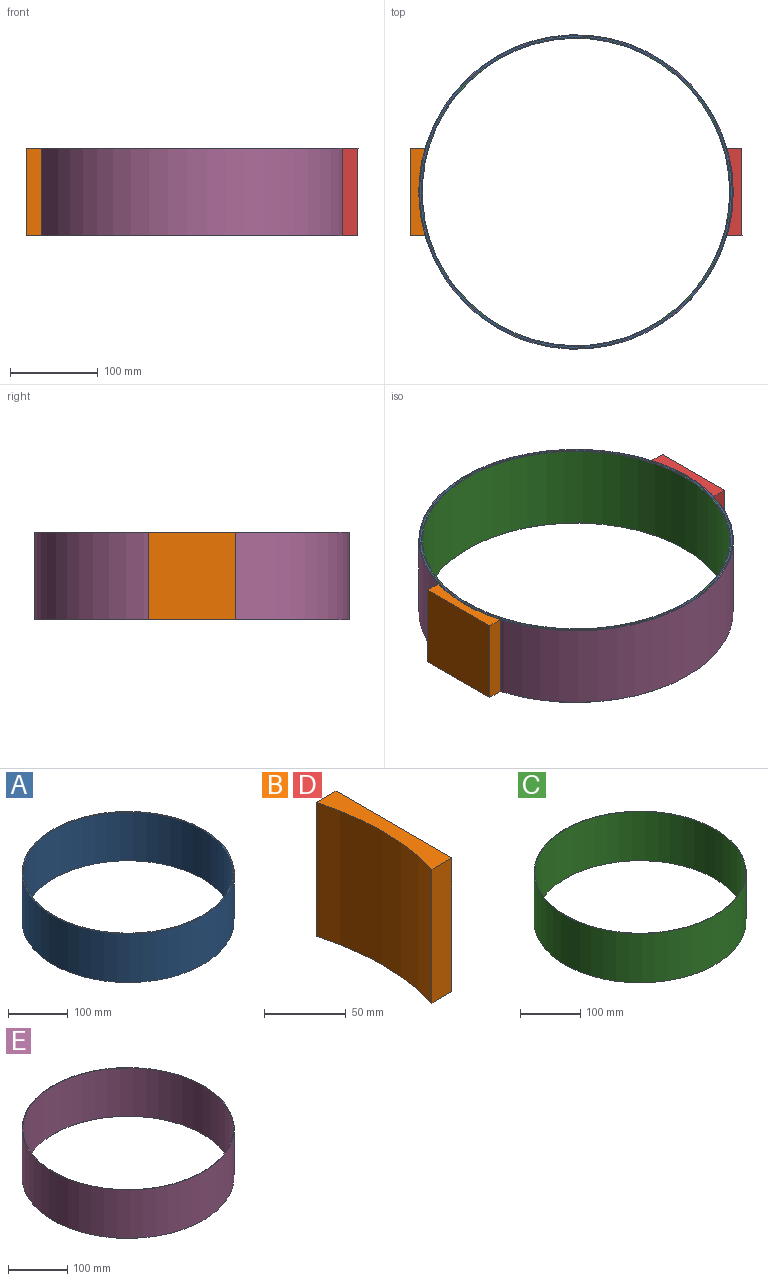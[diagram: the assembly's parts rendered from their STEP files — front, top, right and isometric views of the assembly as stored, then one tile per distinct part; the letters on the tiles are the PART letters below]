
ASSEMBLY  parts=5 mates=7
PART A: 4 faces, bbox 356x356x100 mm
  f0: cylinder r=176mm len=352mm, axis (0,0,-1), area 110584.1mm2, adj f2,f3
  f1: cylinder r=178mm len=356mm, axis (0,0,-1), area 111840.7mm2, adj f2,f3
  f2: plane 356x356mm, normal (0,0,1), area 2224.2mm2, adj f0,f1
  f3: plane 356x356mm, normal (0,0,-1), area 2224.2mm2, adj f0,f1
PART B: 6 faces, bbox 17.1x100x100 mm
  f0: plane 100x100mm, normal (1,0,0), area 10000mm2, adj f1,f3,f4,f5
  f1: plane 100x17.13mm, normal (0,1,0), area 1712.5mm2, adj f0,f2,f4,f5
  f2: cylinder r=179mm len=100mm, axis (0,0,-1), area 10134.8mm2, adj f1,f3,f4,f5
  f3: plane 100x17.13mm, normal (0,-1,0), area 1712.5mm2, adj f0,f2,f4,f5
  f4: plane 100x17.13mm, normal (0,0,1), area 1235.6mm2, adj f0,f1,f2,f3
  f5: plane 100x17.13mm, normal (0,0,-1), area 1235.6mm2, adj f0,f1,f2,f3
PART C: 4 faces, bbox 352x352x100 mm
  f0: cylinder r=175mm len=350mm, axis (0,0,-1), area 109955.7mm2, adj f2,f3
  f1: cylinder r=176mm len=352mm, axis (0,0,-1), area 110584.1mm2, adj f2,f3
  f2: plane 352x352mm, normal (0,0,1), area 1102.7mm2, adj f0,f1
  f3: plane 352x352mm, normal (0,0,-1), area 1102.7mm2, adj f0,f1
PART D: same geometry as B
PART E: 4 faces, bbox 358x358x100 mm
  f0: cylinder r=178mm len=356mm, axis (0,0,-1), area 111840.7mm2, adj f2,f3
  f1: cylinder r=179mm len=358mm, axis (0,0,-1), area 112469mm2, adj f2,f3
  f2: plane 358x358mm, normal (0,0,1), area 1121.5mm2, adj f0,f1
  f3: plane 358x358mm, normal (0,0,-1), area 1121.5mm2, adj f0,f1
PLACE A rot(axis=(-0.66,0.11,0.74),0deg) t=(-101.08,289.06,423.98)mm
PLACE B rot(axis=(0,0,-1),180deg) t=(-101.08,289.06,423.98)mm
PLACE C rot(axis=(-0.66,0.11,0.74),0deg) t=(-101.08,289.06,423.98)mm
PLACE D rot(axis=(-0.66,0.11,0.74),0deg) t=(-101.08,289.06,423.98)mm
PLACE E rot(axis=(-0.66,0.11,0.74),0deg) t=(-101.08,289.06,423.98)mm fixed
MATE fastened A.f0 <-> C.f0  axis (0,0,1) through (-101.08,289.06,523.98)mm
MATE planar B.f4 <-> D.f4  axis (0,0,1) through (-283.72,289.06,523.98)mm
MATE parallel B.f0 <-> D.f0  axis (-1,0,0) through (-290.08,289.06,473.98)mm
MATE planar B.f4 <-> A.f1  axis (0,0,1) through (-283.72,289.06,523.98)mm
MATE slider D.f2 <-> E.f1  axis (0,0,-1) through (-101.08,289.06,473.98)mm
MATE cylindrical E.f1 <-> B.f2  axis (0,0,-1) through (-101.08,289.06,473.98)mm
MATE fastened C.f0 <-> E.f0  axis (0,0,-1) through (-101.08,289.06,523.98)mm
